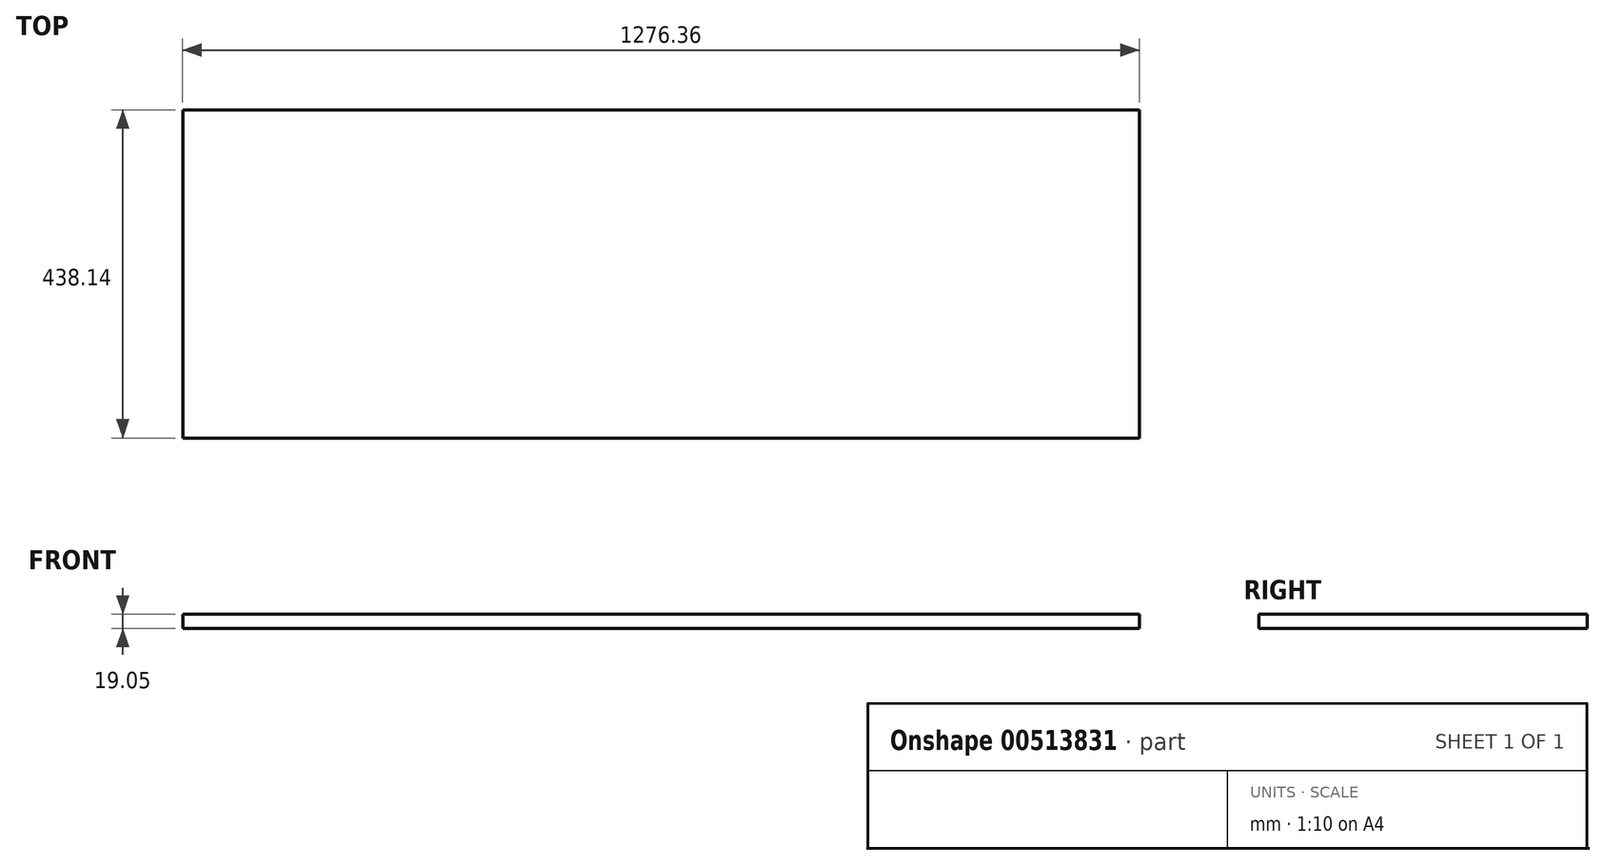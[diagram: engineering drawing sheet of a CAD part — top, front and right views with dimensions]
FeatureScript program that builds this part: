
annotation { "Feature Type Name" : "Feature", "Feature Type Description" : "" }
export const myFeature = defineFeature(function(context is Context, id is Id, definition is map)
    precondition{}
    {
        {
            var Q0;
            Q0=qCreatedBy(makeId("Top.planeOp"),FACE);
            var sketch = newSketch(context, id + "F0", { "sketchPlane" : qUnion([Q0])});
            skLineSegment(sketch, "E0.bottom", {"start": v(638.17, 219.08) * mm, "end": v(-638.18, 219.07) * mm});
            skLineSegment(sketch, "E0.top", {"start": v(638.18, -219.07) * mm, "end": v(-638.17, -219.08) * mm});
            skLineSegment(sketch, "E0.left", {"start": v(638.17, 219.08) * mm, "end": v(638.18, -219.07) * mm});
            skLineSegment(sketch, "E0.right", {"start": v(-638.18, 219.07) * mm, "end": v(-638.17, -219.08) * mm});
            skPoint(sketch, "E0.middle", {"position": v(0, 0) * mm});
            skSolve(sketch);
        }
        {
            var Q0;
            Q0 = qSketchRegion(id + "F0", true);
            extrude(context, id + "F1", {"entities" : qUnion([Q0]), "depth" : 19.05 * mm});
        }
    });
